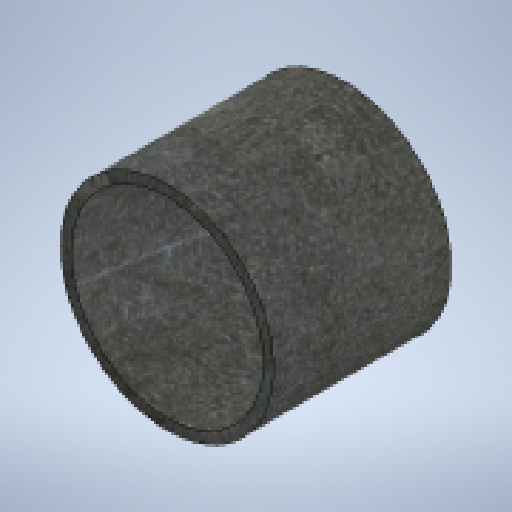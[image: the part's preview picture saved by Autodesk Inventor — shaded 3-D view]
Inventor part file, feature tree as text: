
AUTODESK INVENTOR PART (.ipt)
format: ipt  version: 2025.1 (Build 291241020, 241B)  size: 163,328 bytes
history: native  units: mm
features: extrude x1, sketch x1
ambient origin geometry x8: Origin, YZ Plane, XZ Plane, XY Plane, X Axis, Y Axis, Z Axis, Center Point
bodies: Solid1 (feature_tree)
feature tree (2):
  extrude  "Extrusion1"  Depth=600.0mm
  sketch  "Sketch1"  dims[d0=60.0mm d1=3.0mm d2=600.0mm d3=0.0mm]
